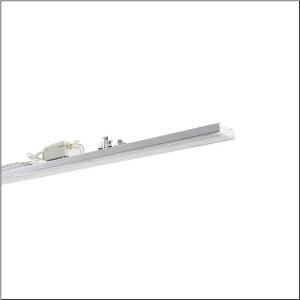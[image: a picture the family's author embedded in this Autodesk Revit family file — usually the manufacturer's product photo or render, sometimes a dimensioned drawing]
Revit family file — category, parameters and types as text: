
# Revit family: licross_r__21_recessed_mo_52tl1edn465g_00db
name_source: partatom
category: Lighting Fixtures
units: mm (PartAtom-declared; Revit-internal decimal feet)

## family parameters
Cut with Voids When Loaded = No
Host = Face
Light Source = No
Part Type = Normal
Room Calculation Point = No
Round Connector Dimension = Use Diameter
Shared = No

## types (1)
- --- (1 x LED, 6990 lm, 39.3 W, 4000K)
    Apparent Load = 39 VA
    CIE Flux Codes = 85 95 99 100 100
    Color Rendering = 80
    Color Temperature = 4000K
    Default Elevation = 1800 mm
    Description = Licross® 21 Recessed MO, luminaire insert, of sheet steel, galvanised, coil coated, white, length: 1.500mm, width: 66mm, height: 67mm, LED rated luminous flux: 6.990lm, light colour: 840, control gear: DALI 2, with plug, 5-pole, with phase selection, mains connection: 220..240V, AC, 50/60Hz, rated input power: 39W, halogen-free wiring, primary light control with lens, of plastic, primary optical cover: cover, of PMMA, light emission: direct distribution, primary light characteristic: symmetric, protection rating (complete): IP40, insulation class (complete): insulation class I (protective earthing), certification: CE, ENEC, VDE, UKCA, protection symbol: D if used in an environment without relevant dust loads with corresponding accessories, impact resistance: IK06, permissible ambient temperature for indoor applications: -25..+40°C, corresponds to IFS (International Featured Standards) requirements for safety and quality in the food industry, reducing of maximum allowable ambient temperature of 5°C with ceiling mounting, LABS conformity tested according to VDMA 24364:2018-05, packaging unit: 1 piece
    Height = 58 mm
    Lamp = 1 x LED
    Lamp Light Flux = 6990 lm
    Lamp Power = 39.3 W
    Lamp count = 1
    Length = 1500 mm
    Luminous efficacy = 178 lm/W
    Manufacturer = Siteco
    ModVariant = No
    Model = 52TL1EDN465G
    Mounting Place = Ceiling
    Mounting Type = Pendant
    Number of Poles = 1
    OnlyDefault = Yes
    Power Factor = 1
    Product Name = Licross® 21 Recessed MO
    Product group = luminaire insert
    ProductGroupID = 901
    Protection Class = Protection class I
    Protection Degree = IP 40
    RLX_Detail_Level = 1
    RLX_Emergency_Light_Flux = 0 lm
    RLX_Emergency_Type = 0
    RLX_Emergency_Type_DB = No
    RlxData = <blob elided: 24217 chars, md5=d2c008b3>
    Socket = socket
    Standby Power = 0 W
    System Light Flux = 6990 lm
    System Power = 39 W
    Type Comments = factory setting: luminous flux: 100 % | dim-lin: 254 | 267 mA
    Type Image = l_1296930.jpg
    URL = http://relux.com
    VarID = @adj_056877
    Voltage = 0 V
    Weight = 0.00 kg
    Width = 66 mm

## geometry (parser evidence)
native form markers: Blend x4, Sweep x12
no freeform markers — native parametric forms only
